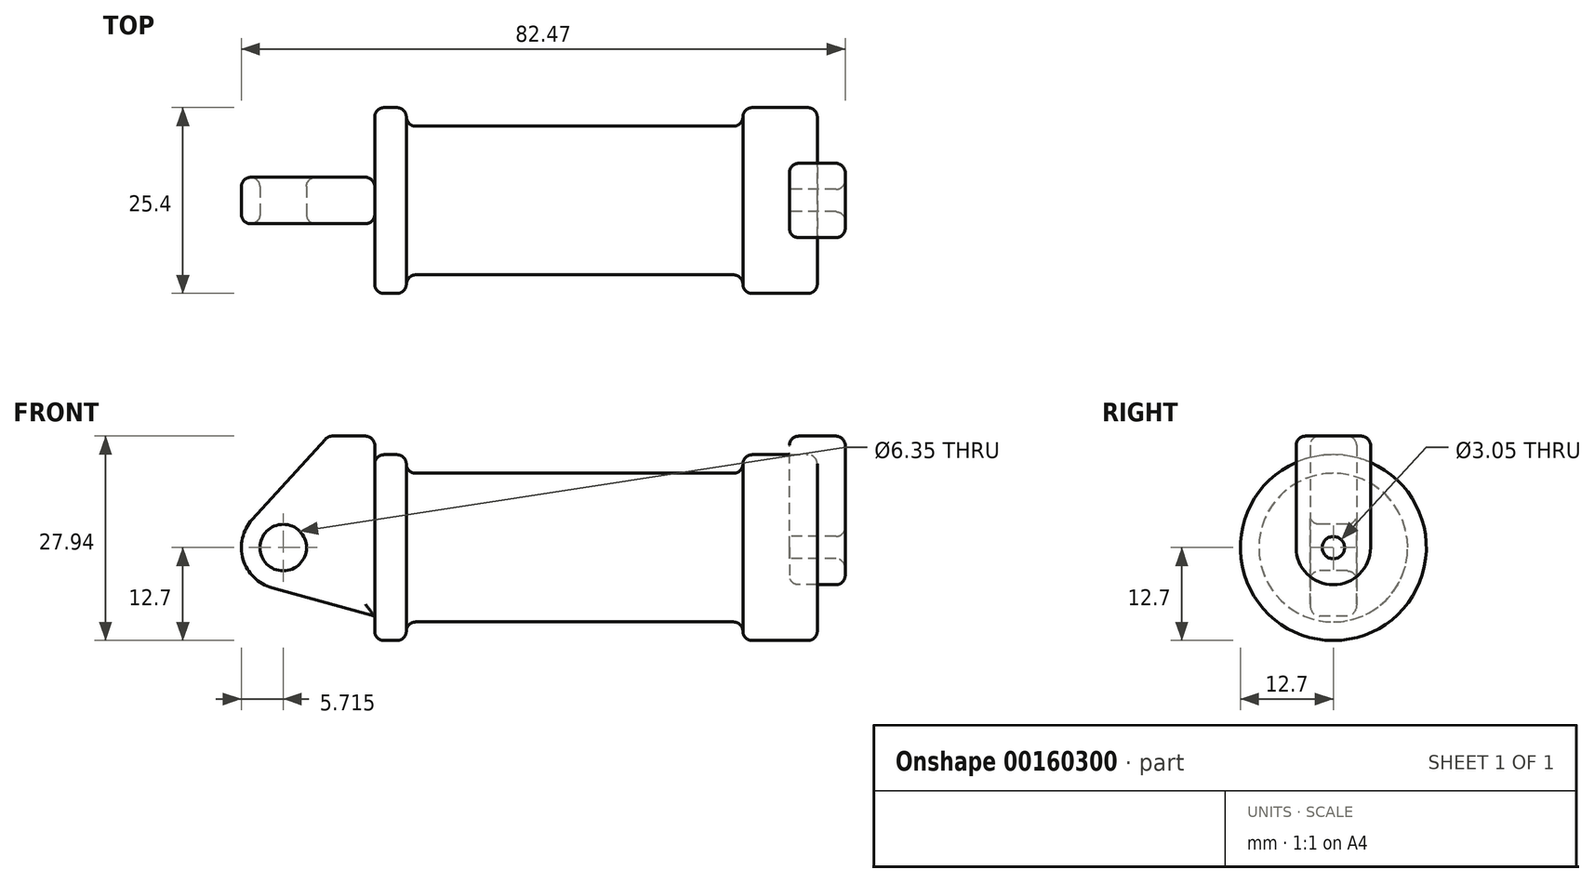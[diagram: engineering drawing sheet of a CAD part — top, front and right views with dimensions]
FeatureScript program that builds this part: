
annotation { "Feature Type Name" : "Feature", "Feature Type Description" : "" }
export const myFeature = defineFeature(function(context is Context, id is Id, definition is map)
    precondition{}
    {
        {
            var Q0;
            Q0=qCreatedBy(makeId("Front.planeOp"),FACE);
            var sketch = newSketch(context, id + "F0", { "sketchPlane" : qUnion([Q0])});
            skLineSegment(sketch, "E0", {"start": v(0, 0) * mm, "end": v(0, 12.7) * mm});
            skLineSegment(sketch, "E1", {"start": v(0, 12.7) * mm, "end": v(10.16, 12.7) * mm});
            skLineSegment(sketch, "E2", {"start": v(10.16, 12.7) * mm, "end": v(10.16, 10.16) * mm});
            skLineSegment(sketch, "E3", {"start": v(10.16, 10.16) * mm, "end": v(56.13, 10.16) * mm});
            skLineSegment(sketch, "E4", {"start": v(56.13, 10.16) * mm, "end": v(56.13, 12.7) * mm});
            skLineSegment(sketch, "E5", {"start": v(56.13, 12.7) * mm, "end": v(66.3, 12.7) * mm});
            skLineSegment(sketch, "E6", {"start": v(66.3, 12.7) * mm, "end": v(66.3, 0) * mm});
            skLineSegment(sketch, "E7", {"start": v(66.3, 0) * mm, "end": v(0, 0) * mm});
            skLineSegment(sketch, "E8", {"start": v(5.84, 15.24) * mm, "end": v(-0.5, 15.24) * mm});
            skLineSegment(sketch, "E9", {"start": v(-0.5, 15.24) * mm, "end": v(-10.88, 3.85) * mm});
            skLineSegment(sketch, "E10", {"start": v(0, 0) * mm, "end": v(-6.65, 0) * mm});
            skCircle(sketch, "E11", {"center": v(-6.65, 0) * mm, "radius": 5.72 * mm});
            skCircle(sketch, "E12", {"center": v(-6.65, 0) * mm, "radius": 3.18 * mm});
            skLineSegment(sketch, "E13", {"start": v(5.84, 15.24) * mm, "end": v(5.84, -9.4) * mm});
            skLineSegment(sketch, "E14", {"start": v(5.84, -9.4) * mm, "end": v(-8.18, -5.5) * mm});
            skSolve(sketch);
        }
        {
            var Q0;
            {var subQ0=sQuery(id+"F0.wireOp",EDGE,"E2");Q0=makeQuery(id+"F0.imprint","IMPRINT",FACE,{"disambiguationData":[TD([[makeQuery(id+"F0.imprint","IMPRINT",EDGE,{"derivedFrom":subQ0}),-1.0]])]});}
            var Q1;
            Q1=sQuery(id+"F0.wireOp",EDGE,"E7");
            revolve(context, id + "F1", {"entities" : qUnion([Q0]), "axis" : qUnion([Q1]), "revolveType" : RevolveType.FULL});
        }
        {
            var Q0;
            Q0=makeQuery(id+"F1.opRevolve","SWEPT_FACE",FACE,{"disambiguationData":[OSD([sQuery(id+"F0.wireOp",EDGE,"E6")])]});
            var sketch = newSketch(context, id + "F2", { "sketchPlane" : qUnion([Q0])});
            skCircle(sketch, "E15", {"center": v(0, 0) * mm, "radius": 1.52 * mm});
            skCircle(sketch, "E16", {"center": v(0, 0) * mm, "radius": 5.08 * mm});
            skLineSegment(sketch, "E17", {"start": v(-5.08, 0) * mm, "end": v(-5.08, 15.24) * mm});
            skLineSegment(sketch, "E18", {"start": v(5.08, 0) * mm, "end": v(5.08, 15.24) * mm});
            skLineSegment(sketch, "E19", {"start": v(-5.08, 15.24) * mm, "end": v(5.08, 15.24) * mm});
            skSolve(sketch);
        }
        {
            var Q0;
            Q0 = qSketchRegion(id + "F2", true);
            extrude(context, id + "F3", {"entities" : qUnion([Q0]), "endBound" : BoundingType.SYMMETRIC, "depth" : 7.62 * mm});
        }
        {
            var Q0;
            {var subQ3=sQuery(id+"F0.wireOp",EDGE,"E0");Q0=makeQuery(id+"F0.imprint","IMPRINT",FACE,{"disambiguationData":[TD([[makeQuery(id+"F0.imprint","IMPRINT",EDGE,{"derivedFrom":subQ3}),1.0]])]});}
            var Q1;
            {var subQ4=sQuery(id+"F0.wireOp",EDGE,"E12");Q1=makeQuery(id+"F0.imprint","IMPRINT",FACE,{"disambiguationData":[TD([[makeQuery(id+"F0.imprint","IMPRINT",EDGE,{"derivedFrom":subQ4}),-1.0]])]});}
            var Q2;
            {var subQ0=sQuery(id+"F0.wireOp",EDGE,"E14");Q2=makeQuery(id+"F0.imprint","IMPRINT",FACE,{"disambiguationData":[TD([[makeQuery(id+"F0.imprint","IMPRINT",EDGE,{"derivedFrom":subQ0}),-1.0]])]});}
            var Q3;
            {var subQ0=sQuery(id+"F0.wireOp",EDGE,"E0");Q3=makeQuery(id+"F0.imprint","IMPRINT",FACE,{"disambiguationData":[TD([[makeQuery(id+"F0.imprint","IMPRINT",EDGE,{"derivedFrom":subQ0}),-1.0]])]});}
            extrude(context, id + "F4", {"entities" : qUnion([Q0, Q1, Q2, Q3]), "endBound" : BoundingType.SYMMETRIC, "oppositeDirection" : true, "depth" : 6.35 * mm});
        }
        {
            var Q0;
            Q0=makeQuery(id+"F3.opExtrude","SWEPT_EDGE",EDGE,{"disambiguationData":[OSD([sQuery(id+"F2.wireOp",EDGE,"E17"),sQuery(id+"F2.wireOp",EDGE,"E19")])]});
            var Q1;
            Q1=makeQuery(id+"F3.opExtrude","CAP_EDGE",EDGE,{"disambiguationData":[OSD([sQuery(id+"F2.wireOp",EDGE,"E17")])],"isStart":true});
            var Q2;
            Q2=makeQuery(id+"F3.opExtrude","SWEPT_FACE",FACE,{"disambiguationData":[OSD([sQuery(id+"F2.wireOp",EDGE,"E17")])]});
            var Q3;
            Q3=makeQuery(id+"F3.opExtrude","CAP_FACE",FACE,{"disambiguationData":[OSD([sQuery(id+"F2.wireOp",EDGE,"E15"),sQuery(id+"F2.wireOp",EDGE,"E16"),sQuery(id+"F2.wireOp",EDGE,"E17"),sQuery(id+"F2.wireOp",EDGE,"E18"),sQuery(id+"F2.wireOp",EDGE,"E19")])],"isStart":false});
            var Q4;
            Q4=makeQuery(id+"F3.opExtrude","SWEPT_FACE",FACE,{"disambiguationData":[OSD([sQuery(id+"F2.wireOp",EDGE,"E19")])]});
            var Q5;
            Q5=makeQuery(id+"F1.opRevolve","SWEPT_FACE",FACE,{"disambiguationData":[OSD([sQuery(id+"F0.wireOp",EDGE,"E5")])]});
            var Q6;
            Q6=makeQuery(id+"F1.opRevolve","SWEPT_FACE",FACE,{"disambiguationData":[OSD([sQuery(id+"F0.wireOp",EDGE,"E3")])]});
            var Q7;
            Q7=makeQuery(id+"F4.opExtrude","SWEPT_FACE",FACE,{"disambiguationData":[OSD([sQuery(id+"F0.wireOp",EDGE,"E8")])]});
            var Q8;
            Q8=makeQuery(id+"F4.opExtrude","CAP_FACE",FACE,{"disambiguationData":[OSD([sQuery(id+"F0.wireOp",EDGE,"E8"),sQuery(id+"F0.wireOp",EDGE,"E9"),sQuery(id+"F0.wireOp",EDGE,"E11"),sQuery(id+"F0.wireOp",EDGE,"E12"),sQuery(id+"F0.wireOp",EDGE,"E13"),sQuery(id+"F0.wireOp",EDGE,"E14")])],"isStart":true});
            var Q9;
            Q9=makeQuery(id+"F1.opRevolve","SWEPT_FACE",FACE,{"disambiguationData":[OSD([sQuery(id+"F0.wireOp",EDGE,"E1")])]});
            var Q10;
            Q10=makeQuery(id+"F4.opExtrude","CAP_FACE",FACE,{"disambiguationData":[OSD([sQuery(id+"F0.wireOp",EDGE,"E8"),sQuery(id+"F0.wireOp",EDGE,"E9"),sQuery(id+"F0.wireOp",EDGE,"E11"),sQuery(id+"F0.wireOp",EDGE,"E12"),sQuery(id+"F0.wireOp",EDGE,"E13"),sQuery(id+"F0.wireOp",EDGE,"E14")])],"isStart":false});
            var Q11;
            Q11=makeQuery(id+"F1.opRevolve","SWEPT_FACE",FACE,{"disambiguationData":[OSD([sQuery(id+"F0.wireOp",EDGE,"E13")])]});
            fillet(context, id + "F5", {"entities" : qUnion([Q0, Q1, Q2, Q3, Q4, Q5, Q6, Q7, Q8, Q9, Q10, Q11]), "radius" : 1.27 * mm, "tangentPropagation" : true, "allowEdgeOverflow" : false});
        }
    });
